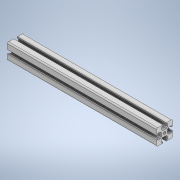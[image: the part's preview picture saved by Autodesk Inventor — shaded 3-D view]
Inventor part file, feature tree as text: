
AUTODESK INVENTOR PART (.ipt)
format: ipt  version: 2020.2 (Build 242310000, 310)  size: 178,176 bytes
history: native  units: in
note: dims shown in document units (in); Inventor stores cm internally (conversion verified against a paired STEP export)
features: extrude x1, sketch x1
ambient origin geometry x8: Origin, YZ Plane, XZ Plane, XY Plane, X Axis, Y Axis, Z Axis, Center Point
bodies: Solid1 (feature_tree)
feature tree (2):
  extrude  "Extrusion1"  Depth=0.29in
  sketch  "Sketch2"  dims[d9=0.2325in d18=0.055in d20=0.055in d34=0.29in d35=0.055in d37=0.058in d38=0.1225in d39=0.081in d40=135.0deg d41=0.17in d42=0.081in d43=0.058in d44=0.055in d45=0.75in d46=0.055in d47=1.5748in d49=360.0deg d51=0.2348in d52=0.232in d56=0.75in d58=0.125in d61=0.055in d62=0.055in d63=0.055in d64=0.055in d65=1.5748in d67=360.0deg d69=7.0in d70=0.0in d71=0.1225in]
